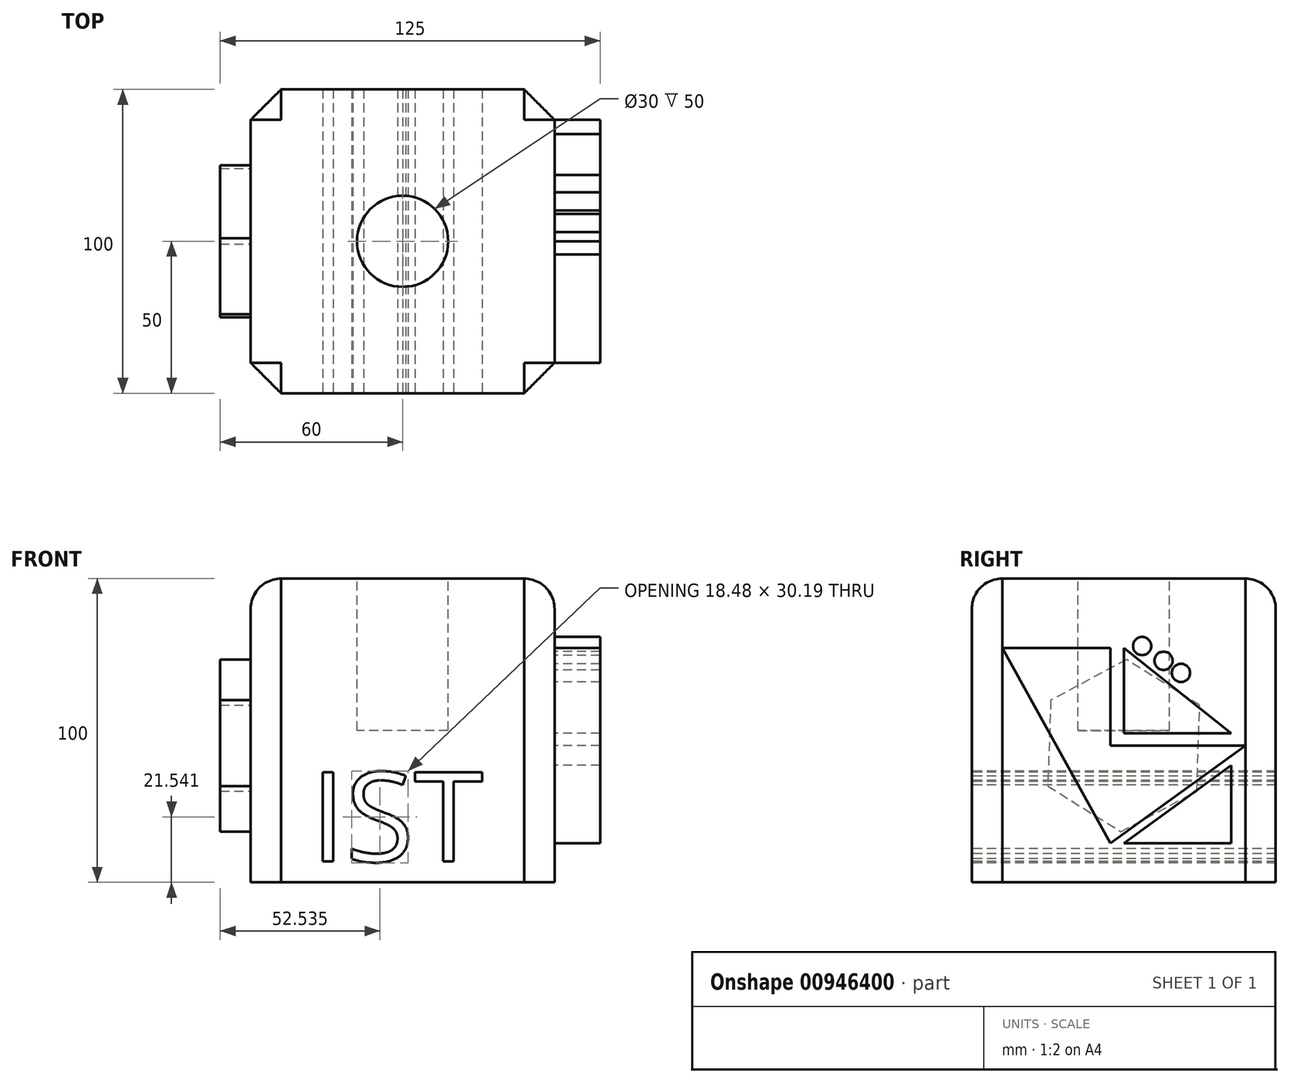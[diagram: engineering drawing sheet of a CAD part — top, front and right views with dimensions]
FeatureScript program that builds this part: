
annotation { "Feature Type Name" : "Feature", "Feature Type Description" : "" }
export const myFeature = defineFeature(function(context is Context, id is Id, definition is map)
    precondition{}
    {
        {
            var Q0;
            Q0=qCreatedBy(makeId("Top.planeOp"),FACE);
            var sketch = newSketch(context, id + "F0", { "sketchPlane" : qUnion([Q0])});
            skLineSegment(sketch, "E0.bottom", {"start": v(-50, 50) * mm, "end": v(50, 50) * mm});
            skLineSegment(sketch, "E0.top", {"start": v(-50, -50) * mm, "end": v(50, -50) * mm});
            skLineSegment(sketch, "E0.left", {"start": v(-50, 50) * mm, "end": v(-50, -50) * mm});
            skLineSegment(sketch, "E0.right", {"start": v(50, 50) * mm, "end": v(50, -50) * mm});
            skPoint(sketch, "E0.middle", {"position": v(0, 0) * mm});
            skSolve(sketch);
        }
        {
            var Q0;
            Q0 = qSketchRegion(id + "F0", true);
            extrude(context, id + "F1", {"entities" : qUnion([Q0]), "depth" : 100 * mm, "offsetDistance" : 25 * mm});
        }
        {
            var Q0;
            Q0=makeQuery(id+"F1.opExtrude","CAP_FACE",FACE,{"disambiguationData":[OSD([sQuery(id+"F0.wireOp",EDGE,"E0.bottom"),sQuery(id+"F0.wireOp",EDGE,"E0.top"),sQuery(id+"F0.wireOp",EDGE,"E0.left"),sQuery(id+"F0.wireOp",EDGE,"E0.right")])],"isStart":false});
            var sketch = newSketch(context, id + "F2", { "sketchPlane" : qUnion([Q0])});
            skCircle(sketch, "E1", {"center": v(0, 0) * mm, "radius": 15 * mm});
            skSolve(sketch);
        }
        {
            var Q0;
            Q0 = qSketchRegion(id + "F2", true);
            extrude(context, id + "F3", {"entities" : qUnion([Q0]), "operationType" : NewBodyOperationType.REMOVE, "oppositeDirection" : true, "depth" : 50 * mm, "offsetDistance" : 25 * mm});
        }
        {
            var Q0;
            Q0=makeQuery(id+"F1.opExtrude","CAP_EDGE",EDGE,{"disambiguationData":[OSD([sQuery(id+"F0.wireOp",EDGE,"E0.top")])],"isStart":false});
            var Q1;
            Q1=makeQuery(id+"F1.opExtrude","CAP_EDGE",EDGE,{"disambiguationData":[OSD([sQuery(id+"F0.wireOp",EDGE,"E0.left")])],"isStart":false});
            var Q2;
            Q2=makeQuery(id+"F1.opExtrude","CAP_EDGE",EDGE,{"disambiguationData":[OSD([sQuery(id+"F0.wireOp",EDGE,"E0.bottom")])],"isStart":false});
            var Q3;
            Q3=makeQuery(id+"F1.opExtrude","CAP_EDGE",EDGE,{"disambiguationData":[OSD([sQuery(id+"F0.wireOp",EDGE,"E0.right")])],"isStart":false});
            fillet(context, id + "F4", {"entities" : qUnion([Q0, Q1, Q2, Q3]), "radius" : 10 * mm, "tangentPropagation" : true, "allowEdgeOverflow" : false});
        }
        {
            var Q0;
            Q0=makeQuery(id+"F1.opExtrude","SWEPT_EDGE",EDGE,{"disambiguationData":[OSD([sQuery(id+"F0.wireOp",EDGE,"E0.top"),sQuery(id+"F0.wireOp",EDGE,"E0.left")])]});
            var Q1;
            Q1=makeQuery(id+"F1.opExtrude","SWEPT_EDGE",EDGE,{"disambiguationData":[OSD([sQuery(id+"F0.wireOp",EDGE,"E0.top"),sQuery(id+"F0.wireOp",EDGE,"E0.right")])]});
            var Q2;
            Q2=makeQuery(id+"F1.opExtrude","SWEPT_EDGE",EDGE,{"disambiguationData":[OSD([sQuery(id+"F0.wireOp",EDGE,"E0.bottom"),sQuery(id+"F0.wireOp",EDGE,"E0.left")])]});
            var Q3;
            Q3=makeQuery(id+"F1.opExtrude","SWEPT_EDGE",EDGE,{"disambiguationData":[OSD([sQuery(id+"F0.wireOp",EDGE,"E0.bottom"),sQuery(id+"F0.wireOp",EDGE,"E0.right")])]});
            chamfer(context, id + "F5", {"entities" : qUnion([Q0, Q1, Q2, Q3]), "width" : 10 * mm, "tangentPropagation" : true});
        }
        {
            var Q0;
            Q0=makeQuery(id+"F1.opExtrude","SWEPT_FACE",FACE,{"disambiguationData":[OSD([sQuery(id+"F0.wireOp",EDGE,"E0.left")])]});
            var sketch = newSketch(context, id + "F6", { "sketchPlane" : qUnion([Q0])});
            skCircle(sketch, "E2.cCircle", {"center": v(0, 45) * mm, "radius": 24.52 * mm, "construction": true});
            skPoint(sketch, "E2.cCircle.centerSnap0", {"position": v(-40, 45) * mm});
            skPoint(sketch, "E2.cCircle.centerSnap1", {"position": v(0, 90) * mm});
            skLineSegment(sketch, "E2.0", {"start": v(-24.98, 58.32) * mm, "end": v(-0.95, 73.3) * mm});
            skLineSegment(sketch, "E2.1", {"start": v(-0.95, 73.3) * mm, "end": v(24.03, 59.97) * mm});
            skLineSegment(sketch, "E2.2", {"start": v(24.03, 59.97) * mm, "end": v(24.98, 31.68) * mm});
            skLineSegment(sketch, "E2.3", {"start": v(24.98, 31.68) * mm, "end": v(0.95, 16.7) * mm});
            skLineSegment(sketch, "E2.4", {"start": v(0.95, 16.7) * mm, "end": v(-24.03, 30.03) * mm});
            skLineSegment(sketch, "E2.5", {"start": v(-24.03, 30.03) * mm, "end": v(-24.98, 58.32) * mm});
            skPoint(sketch, "E2.0.midPoint", {"position": v(-12.96, 65.8) * mm});
            skSolve(sketch);
        }
        {
            var Q0;
            Q0 = qSketchRegion(id + "F6", true);
            extrude(context, id + "F7", {"entities" : qUnion([Q0]), "operationType" : NewBodyOperationType.ADD, "depth" : 10 * mm, "offsetDistance" : 25 * mm});
        }
        {
            var Q0;
            Q0=makeQuery(id+"F1.opExtrude","SWEPT_FACE",FACE,{"disambiguationData":[OSD([sQuery(id+"F0.wireOp",EDGE,"E0.top")])]});
            var sketch = newSketch(context, id + "F8", { "sketchPlane" : qUnion([Q0])});
            skText(sketch, "E3", { "text": "IST", "fontName": "OpenSans-Regular.ttf"});
            const initialGuessF8  = {"E3": [-0.0303, 0.00685, 1, 0, 0.02962]};
            skSetInitialGuess(sketch, initialGuessF8);
            skSolve(sketch);
        }
        {
            var Q0;
            Q0 = qSketchRegion(id + "F8", true);
            extrude(context, id + "F9", {"entities" : qUnion([Q0]), "operationType" : NewBodyOperationType.REMOVE, "oppositeDirection" : true, "depth" : 100 * mm, "offsetDistance" : 25 * mm});
        }
        {
            var Q0;
            Q0=makeQuery(id+"F1.opExtrude","SWEPT_FACE",FACE,{"disambiguationData":[OSD([sQuery(id+"F0.wireOp",EDGE,"E0.right")])]});
            var sketch = newSketch(context, id + "F10", { "sketchPlane" : qUnion([Q0])});
            skLineSegment(sketch, "E4", {"start": v(-4.33, 77.18) * mm, "end": v(-4.33, 12.92) * mm});
            skLineSegment(sketch, "E5", {"start": v(-4.33, 12.92) * mm, "end": v(40, 45.05) * mm});
            skPoint(sketch, "E5.endSnap0", {"position": v(-4.33, 45.05) * mm});
            skLineSegment(sketch, "E6", {"start": v(40, 45.05) * mm, "end": v(-4.33, 45.05) * mm});
            skLineSegment(sketch, "E7", {"start": v(-4.33, 77.18) * mm, "end": v(-40, 77.18) * mm});
            skLineSegment(sketch, "E8", {"start": v(-40, 77.18) * mm, "end": v(-4.33, 12.92) * mm});
            skLineSegment(sketch, "E9", {"start": v(0, 77.18) * mm, "end": v(0, 49.07) * mm});
            skLineSegment(sketch, "E10", {"start": v(0, 49.07) * mm, "end": v(35.36, 49.07) * mm});
            skLineSegment(sketch, "E11", {"start": v(0, 77.18) * mm, "end": v(35.36, 49.07) * mm});
            skLineSegment(sketch, "E12", {"start": v(35.36, 12.92) * mm, "end": v(0, 12.92) * mm});
            skLineSegment(sketch, "E13", {"start": v(0, 12.92) * mm, "end": v(35.36, 38.55) * mm});
            skLineSegment(sketch, "E14", {"start": v(35.36, 38.55) * mm, "end": v(35.36, 12.92) * mm});
            skCircle(sketch, "E15", {"center": v(6.04, 77.77) * mm, "radius": 3 * mm});
            skCircle(sketch, "E16", {"center": v(13.1, 72.94) * mm, "radius": 3 * mm});
            skCircle(sketch, "E17", {"center": v(18.84, 68.93) * mm, "radius": 3 * mm});
            skSolve(sketch);
        }
        {
            var Q0;
            Q0 = qSketchRegion(id + "F10", true);
            extrude(context, id + "F11", {"entities" : qUnion([Q0]), "operationType" : NewBodyOperationType.ADD, "depth" : 15 * mm, "offsetDistance" : 25 * mm});
        }
    });
